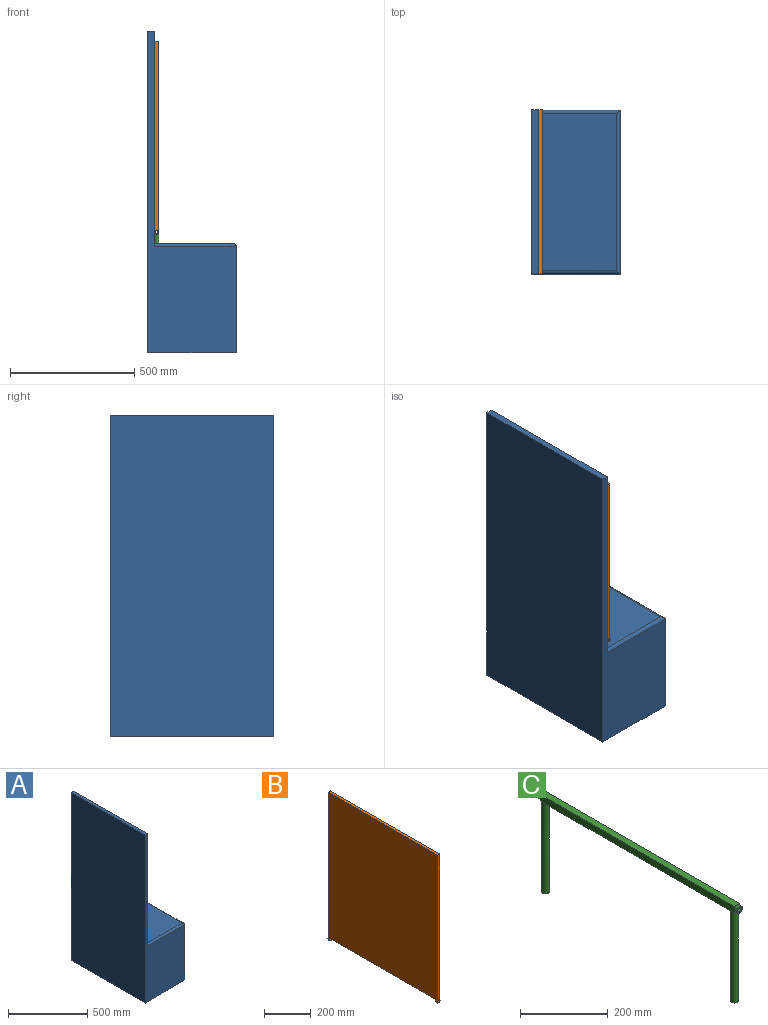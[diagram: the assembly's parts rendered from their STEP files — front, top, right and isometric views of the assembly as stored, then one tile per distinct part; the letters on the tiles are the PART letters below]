
ASSEMBLY  parts=3 mates=2
PART A: 15 faces, bbox 355.6x660.4x1295.4 mm
  f0: plane 1295.4x660.4mm, normal (-1,0,0), area 855482.2mm2, adj f1,f3,f4,f5
  f1: plane 1295.4x355.6mm, normal (0,-1,0), area 173997.6mm2, adj f0,f2,f4,f5,f6,f13
  f2: plane 868.1x660.4mm, normal (1,0,0), area 564975.4mm2, adj f1,f3,f4,f7,f12,f13
  f3: plane 1295.4x355.6mm, normal (0,1,0), area 173997.6mm2, adj f0,f2,f4,f5,f6,f12
  f4: plane 660.4x25.4mm, normal (0,0,1), area 16774.2mm2, adj f0,f1,f2,f3
  f5: plane 660.4x355.6mm, normal (0,0,-1), area 234838.2mm2, adj f0,f1,f3,f6
  f6: plane 660.4x427.3mm, normal (1,0,0), area 282188.9mm2, adj f1,f3,f5,f14
  f7: plane 635x317.5mm, normal (0,0,1), area 201042.5mm2, adj f2,f8,f10,f12,f13,f14
  f8: cylinder r=9.53mm len=256.54mm, axis (0,0,1), area 15353.2mm2, adj f7,f9
  f9: plane 19.05x19.05mm, normal (0,0,1), area 285mm2, adj f8
  f10: cylinder r=9.53mm len=256.54mm, axis (0,0,1), area 15353.2mm2, adj f7,f11
  f11: plane 19.05x19.05mm, normal (0,0,1), area 285mm2, adj f10
  f12: cylinder r=12.7mm len=330.2mm, axis (1,0,0), area 6495.1mm2, adj f2,f3,f7,f14
  f13: cylinder r=12.7mm len=330.2mm, axis (-1,0,0), area 6495.1mm2, adj f1,f2,f7,f14
  f14: cylinder r=12.7mm len=660.4mm, axis (0,-1,0), area 12990.3mm2, adj f6,f7,f12,f13
PART B: 12 faces, bbox 17.8x660.4x777.2 mm
  f0: cylinder r=8.89mm len=17.78mm, axis (0,-1,0), area 331.3mm2, adj f1,f3,f5
  f1: plane 17.78x15.24mm, normal (0,1,0), area 99.9mm2, adj f0,f2,f5
  f2: cylinder r=6.35mm len=12.7mm, axis (0,-1,0), area 314.2mm2, adj f1,f3
  f3: plane 777.24x17.78mm, normal (0,-1,0), area 9777.3mm2, adj f0,f2,f4,f5,f6,f7
  f4: plane 762x660.4mm, normal (-1,0,0), area 503224.8mm2, adj f3,f5,f7,f11
  f5: plane 660.4x12.7mm, normal (0,0,-1), area 8191.1mm2, adj f0,f1,f3,f4,f6,f8,f9,f11
  f6: plane 762x660.4mm, normal (1,0,0), area 503224.8mm2, adj f3,f5,f7,f11
  f7: plane 660.4x12.7mm, normal (0,0,1), area 8387.1mm2, adj f3,f4,f6,f11
  f8: cylinder r=8.89mm len=17.78mm, axis (0,1,0), area 331.3mm2, adj f5,f9,f11
  f9: plane 17.78x15.24mm, normal (0,-1,0), area 99.9mm2, adj f5,f8,f10
  f10: cylinder r=6.35mm len=12.7mm, axis (0,1,0), area 314.2mm2, adj f9,f11
  f11: plane 777.24x17.78mm, normal (0,1,0), area 9777.3mm2, adj f4,f5,f6,f7,f8,f10
PART C: 25 faces, bbox 17.8x643.1x271.8 mm
  f0: plane 8.89x8.89mm, normal (0,-1,0), area 17mm2, adj f7,f10,f12
  f1: plane 8.89x8.89mm, normal (0,-1,0), area 17mm2, adj f10,f11,f12
  f2: plane 8.89x8.89mm, normal (0,-1,0), area 17mm2, adj f8,f11,f12
  f3: cylinder r=8.89mm len=254mm, axis (0,0,-1), area 14187.8mm2, adj f4,f5,f6,f7
  f4: plane 17.78x17.78mm, normal (0,0,-1), area 248.3mm2, adj f3
  f5: plane 609.6x17.78mm, normal (0,0,-1), area 10590.4mm2, adj f3,f8,f10,f17
  f6: plane 8.89x8.89mm, normal (0,0,-1), area 17mm2, adj f3,f8,f9
  f7: plane 8.89x8.89mm, normal (0,0,-1), area 17mm2, adj f0,f3,f10
  f8: plane 627.38x17.78mm, normal (-1,0,0), area 11154.8mm2, adj f2,f5,f6,f9,f11,f16,f19,f21
  f9: plane 8.89x8.89mm, normal (0,-1,0), area 17mm2, adj f6,f8,f12
  f10: plane 627.38x17.78mm, normal (1,0,0), area 11154.8mm2, adj f0,f1,f5,f7,f11,f14,f15,f20
  f11: plane 627.38x17.78mm, normal (0,0,1), area 11154.8mm2, adj f1,f2,f8,f10,f15,f16
  f12: cylinder r=8.89mm len=17.78mm, axis (0,1,0), area 439.8mm2, adj f0,f1,f2,f9,f13
  f13: plane 17.78x17.78mm, normal (0,-1,0), area 121.6mm2, adj f12,f24
  f14: plane 8.89x8.89mm, normal (0,1,0), area 17mm2, adj f10,f20,f22
  f15: plane 8.89x8.89mm, normal (0,1,0), area 17mm2, adj f10,f11,f22
  f16: plane 8.89x8.89mm, normal (0,1,0), area 17mm2, adj f8,f11,f22
  f17: cylinder r=8.89mm len=254mm, axis (0,0,-1), area 14187.8mm2, adj f5,f18,f19,f20
  f18: plane 17.78x17.78mm, normal (0,0,-1), area 248.3mm2, adj f17
  f19: plane 8.89x8.89mm, normal (0,0,-1), area 17mm2, adj f8,f17,f21
  f20: plane 8.89x8.89mm, normal (0,0,-1), area 17mm2, adj f10,f14,f17
  f21: plane 8.89x8.89mm, normal (0,1,0), area 17mm2, adj f8,f19,f22
  f22: cylinder r=8.89mm len=17.78mm, axis (0,-1,0), area 439.8mm2, adj f14,f15,f16,f21,f23
  f23: plane 17.78x17.78mm, normal (0,1,0), area 121.6mm2, adj f22,f24
  f24: cylinder r=6.35mm len=643.13mm, axis (0,-1,0), area 25659.7mm2, adj f13,f23
PLACE A t=(871.84,619.52,-130.5)mm
PLACE B t=(906.76,949.72,356.07)mm
PLACE C t=(906.76,644.92,93.18)mm
MATE slider C.f3 <-> A.f8  axis (0,0,-1) through (906.76,644.92,220.18)mm
MATE revolute B.f2 <-> C.f12  axis (0,1,0) through (906.76,627.4,356.07)mm
